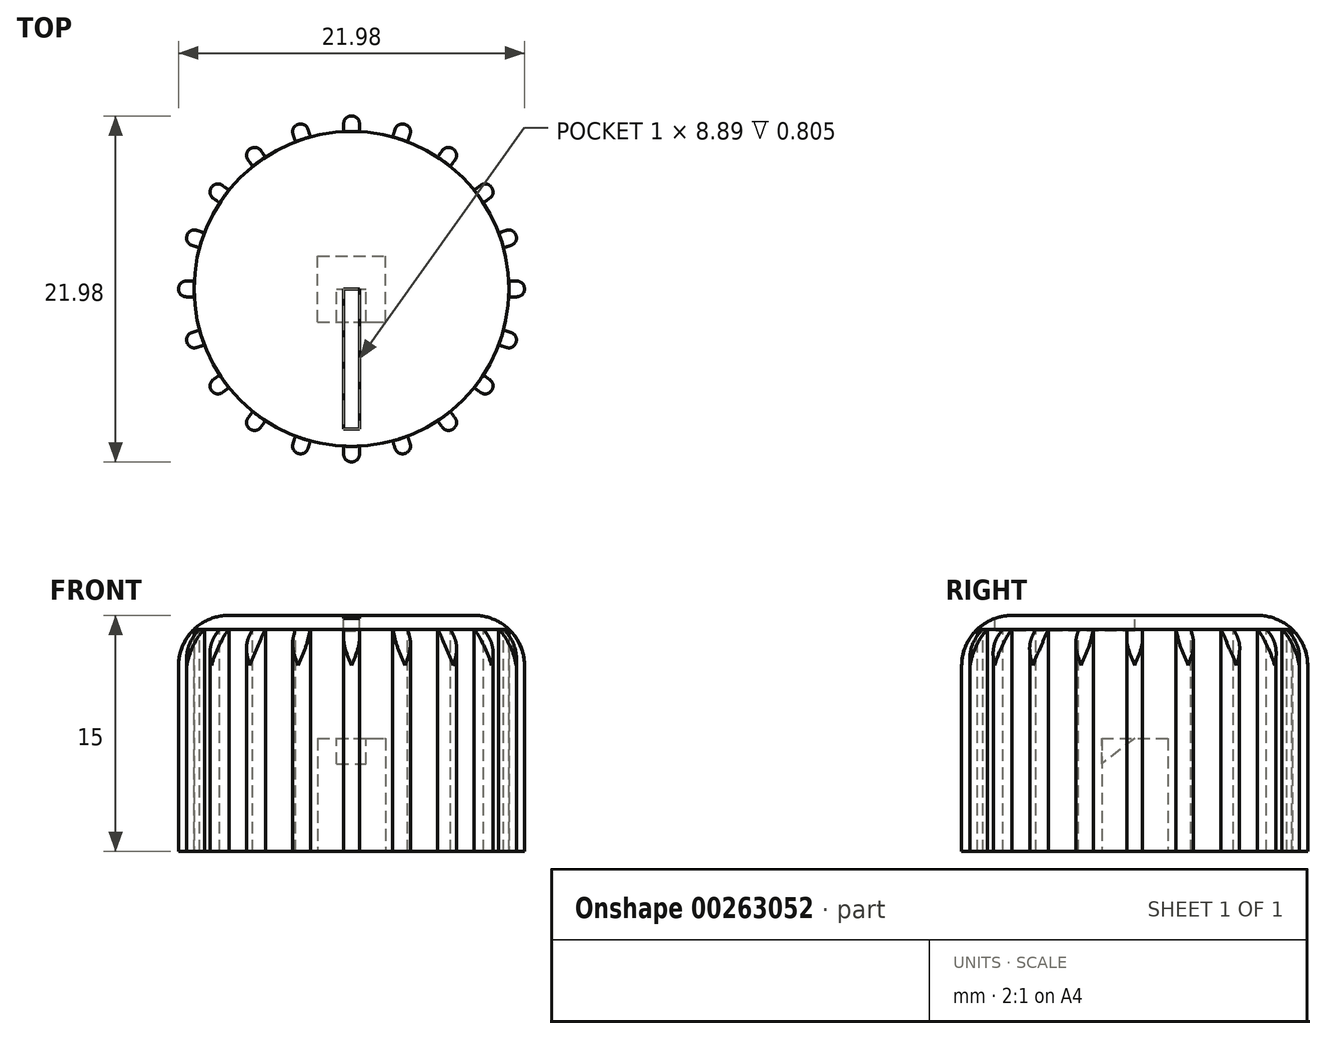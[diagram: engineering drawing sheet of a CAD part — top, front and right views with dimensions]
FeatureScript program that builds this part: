
annotation { "Feature Type Name" : "Feature", "Feature Type Description" : "" }
export const myFeature = defineFeature(function(context is Context, id is Id, definition is map)
    precondition{}
    {
        {
            var Q0;
            Q0=qCreatedBy(makeId("Top.planeOp"),FACE);
            var sketch = newSketch(context, id + "F0", { "sketchPlane" : qUnion([Q0])});
            skCircle(sketch, "E0", {"center": v(0, 0) * mm, "radius": 10 * mm});
            skSolve(sketch);
        }
        {
            var Q0;
            Q0=makeQuery(id+"F0.imprint","IMPRINT",FACE,{"disambiguationData":[TD([[makeQuery(id+"F0.imprint","IMPRINT",EDGE,{"derivedFrom":sQuery(id+"F0.wireOp",EDGE,"E0")}),1.0]])]});
            extrude(context, id + "F1", {"entities" : qUnion([Q0]), "depth" : 15 * mm});
        }
        {
            var Q0;
            Q0=makeQuery(id+"F1.opExtrude","CAP_FACE",FACE,{"disambiguationData":[OSD([sQuery(id+"F0.wireOp",EDGE,"E0")])],"isStart":true});
            var sketch = newSketch(context, id + "F2", { "sketchPlane" : qUnion([Q0])});
            skLineSegment(sketch, "E1.bottom", {"start": v(-2.16, 2.1) * mm, "end": v(2.16, 2.1) * mm});
            skLineSegment(sketch, "E1.top", {"start": v(-2.16, -2.1) * mm, "end": v(2.16, -2.1) * mm});
            skLineSegment(sketch, "E1.left", {"start": v(-2.16, 2.1) * mm, "end": v(-2.16, -2.1) * mm});
            skLineSegment(sketch, "E1.right", {"start": v(2.16, 2.1) * mm, "end": v(2.16, -2.1) * mm});
            skPoint(sketch, "E2", {"position": v(0, 2.1) * mm});
            skPoint(sketch, "E3", {"position": v(2.16, 0) * mm});
            skLineSegment(sketch, "E4.bottom", {"start": v(-0.94, 2.1) * mm, "end": v(0.94, 2.1) * mm});
            skLineSegment(sketch, "E4.top", {"start": v(-0.94, 0) * mm, "end": v(0.94, 0) * mm});
            skLineSegment(sketch, "E4.left", {"start": v(-0.94, 2.1) * mm, "end": v(-0.94, 0) * mm});
            skLineSegment(sketch, "E4.right", {"start": v(0.94, 2.1) * mm, "end": v(0.94, 0) * mm});
            skPoint(sketch, "E5", {"position": v(0, 0) * mm});
            skSolve(sketch);
        }
        {
            var Q0;
            Q0=makeQuery(id+"F2.imprint","IMPRINT",FACE,{"disambiguationData":[TD([[makeQuery(id+"F2.imprint","IMPRINT",EDGE,{"derivedFrom":sQuery(id+"F2.wireOp",EDGE,"E1.top")}),1.0]])]});
            extrude(context, id + "F3", {"entities" : qUnion([Q0]), "operationType" : NewBodyOperationType.REMOVE, "oppositeDirection" : true, "depth" : 1.63 * mm});
        }
        {
            var Q0;
            Q0=makeQuery(id+"F3.boolean.opBoolean","COPY",FACE,{"derivedFrom":makeQuery(id+"F3.opExtrude","CAP_FACE",FACE,{"disambiguationData":[OSD([sQuery(id+"F2.wireOp",EDGE,"E1.bottom"),sQuery(id+"F2.wireOp",EDGE,"E1.top"),sQuery(id+"F2.wireOp",EDGE,"E1.left"),sQuery(id+"F2.wireOp",EDGE,"E1.right"),sQuery(id+"F2.wireOp",EDGE,"E4.top"),sQuery(id+"F2.wireOp",EDGE,"E4.left"),sQuery(id+"F2.wireOp",EDGE,"E4.right")])],"isStart":false})});
            var sketch = newSketch(context, id + "F4", { "sketchPlane" : qUnion([Q0])});
            skLineSegment(sketch, "E6.bottom", {"start": v(-2.16, -2.1) * mm, "end": v(2.16, -2.1) * mm});
            skLineSegment(sketch, "E6.top", {"start": v(-2.16, 2.1) * mm, "end": v(2.16, 2.1) * mm});
            skLineSegment(sketch, "E6.left", {"start": v(-2.16, -2.1) * mm, "end": v(-2.16, 2.1) * mm});
            skLineSegment(sketch, "E6.right", {"start": v(2.16, -2.1) * mm, "end": v(2.16, 2.1) * mm});
            skSolve(sketch);
        }
        {
            var Q0;
            Q0=makeQuery(id+"F4.imprint","IMPRINT",FACE,{"disambiguationData":[TD([[makeQuery(id+"F4.imprint","IMPRINT",EDGE,{"derivedFrom":makeQuery(id+"F3.boolean.opBoolean","COPY",EDGE,{"derivedFrom":makeQuery(id+"F3.opExtrude","CAP_EDGE",EDGE,{"disambiguationData":[OSD([sQuery(id+"F2.wireOp",EDGE,"E4.top")])],"isStart":false})})}),1.0]])]});
            var Q1;
            Q1=makeQuery(id+"F4.imprint","IMPRINT",FACE,{"disambiguationData":[TD([[makeQuery(id+"F4.imprint","IMPRINT",EDGE,{"derivedFrom":sQuery(id+"F4.wireOp",EDGE,"E6.bottom")}),1.0]])]});
            extrude(context, id + "F5", {"entities" : qUnion([Q0, Q1]), "operationType" : NewBodyOperationType.REMOVE, "oppositeDirection" : true, "depth" : 5.56 * mm});
        }
        {
            var Q0;
            Q0=makeQuery(id+"F5.boolean.opBoolean","COPY",FACE,{"derivedFrom":makeQuery(id+"F5.opExtrude","CAP_FACE",FACE,{"disambiguationData":[OSD([sQuery(id+"F4.wireOp",EDGE,"E6.bottom"),sQuery(id+"F4.wireOp",EDGE,"E6.top"),sQuery(id+"F4.wireOp",EDGE,"E6.left"),sQuery(id+"F4.wireOp",EDGE,"E6.right")])],"isStart":false})});
            var sketch = newSketch(context, id + "F6", { "sketchPlane" : qUnion([Q0])});
            skSolve(sketch);
        }
        {
            var Q0;
            Q0=makeQuery(id+"F6.imprint","IMPRINT",FACE,{"disambiguationData":[TD([[makeQuery(id+"F6.imprint","IMPRINT",EDGE,{"derivedFrom":makeQuery(id+"F5.boolean.opBoolean","COPY",EDGE,{"derivedFrom":makeQuery(id+"F5.opExtrude","CAP_EDGE",EDGE,{"disambiguationData":[OSD([sQuery(id+"F4.wireOp",EDGE,"E6.bottom")])],"isStart":false})})}),1.0]])]});
            var sketch = newSketch(context, id + "F7", { "sketchPlane" : qUnion([Q0])});
            skLineSegment(sketch, "E7.0", {"start": v(0.94, 2.1) * mm, "end": v(0.94, 0) * mm});
            skLineSegment(sketch, "E8.0", {"start": v(-0.94, 0) * mm, "end": v(0.94, 0) * mm});
            skLineSegment(sketch, "E9.0", {"start": v(-0.94, 2.1) * mm, "end": v(-0.94, 0) * mm});
            skSolve(sketch);
        }
        {
            var Q0;
            Q0=makeQuery(id+"F3.boolean.opBoolean","COPY",FACE,{"derivedFrom":makeQuery(id+"F3.opExtrude","SWEPT_FACE",FACE,{"disambiguationData":[OSD([sQuery(id+"F2.wireOp",EDGE,"E4.top")])]})});
            var Q1;
            {var subQ0=sQuery(id+"F2.wireOp",EDGE,"E1.bottom");Q1=makeQuery(id+"F5.boolean.opBoolean","MERGE",FACE,{"derivedFrom":[makeQuery(id+"F3.boolean.opBoolean","COPY",FACE,{"derivedFrom":makeQuery(id+"F3.opExtrude","SWEPT_FACE",FACE,{"disambiguationData":[OSD([subQ0]),TDD([makeQuery(id+"F2.imprint","IMPRINT",EDGE,{"disambiguationData":[TD([[makeQuery(id+"F2.imprint","INTERSECT",VERTEX,{"derivedFrom":[subQ0,sQuery(id+"F2.wireOp",EDGE,"E1.left")]}),-1.0]])],"derivedFrom":subQ0})])]})}),makeQuery(id+"F3.boolean.opBoolean","COPY",FACE,{"derivedFrom":makeQuery(id+"F3.opExtrude","SWEPT_FACE",FACE,{"disambiguationData":[OSD([subQ0]),TDD([makeQuery(id+"F2.imprint","IMPRINT",EDGE,{"disambiguationData":[TD([[makeQuery(id+"F2.imprint","INTERSECT",VERTEX,{"derivedFrom":[subQ0,sQuery(id+"F2.wireOp",EDGE,"E1.right")]}),1.0]])],"derivedFrom":subQ0})])]})}),makeQuery(id+"F5.opExtrude","SWEPT_FACE",FACE,{"disambiguationData":[OSD([sQuery(id+"F4.wireOp",EDGE,"E6.top")])]})]});}
            extrude(context, id + "F8", {"entities" : qUnion([Q0]), "operationType" : NewBodyOperationType.REMOVE, "endBound" : BoundingType.UP_TO_SURFACE, "oppositeDirection" : true, "endBoundEntityFace" : qUnion([Q1]), "depth" : 25.4 * mm});
        }
        {
            var Q0;
            {var subQ0=sQuery(id+"F7.wireOp",EDGE,"E7.0");Q0=makeQuery(id+"F7.imprint","IMPRINT",FACE,{"disambiguationData":[TD([[makeQuery(id+"F7.imprint","IMPRINT",EDGE,{"derivedFrom":subQ0}),-1.0]])]});}
            extrude(context, id + "F9", {"entities" : qUnion([Q0]), "operationType" : NewBodyOperationType.ADD, "depth" : 1.63 * mm});
        }
        {
            var Q0;
            Q0=makeQuery(id+"F9.opExtrude","SWEPT_FACE",FACE,{"disambiguationData":[OSD([sQuery(id+"F7.wireOp",EDGE,"E7.0")])]});
            var sketch = newSketch(context, id + "F10", { "sketchPlane" : qUnion([Q0])});
            skLineSegment(sketch, "E10", {"start": v(0, 7.19) * mm, "end": v(-2.1, 5.56) * mm});
            skLineSegment(sketch, "E11", {"start": v(-2.1, 5.56) * mm, "end": v(-2.1, 7.19) * mm});
            skLineSegment(sketch, "E12", {"start": v(-2.1, 7.19) * mm, "end": v(0, 7.19) * mm});
            skLineSegment(sketch, "E13", {"start": v(0, 5.56) * mm, "end": v(0, 7.19) * mm});
            skLineSegment(sketch, "E14", {"start": v(-2.1, 5.56) * mm, "end": v(0, 5.56) * mm});
            skSolve(sketch);
        }
        {
            var Q0;
            Q0=makeQuery(id+"F10.imprint","IMPRINT",FACE,{"disambiguationData":[TD([[makeQuery(id+"F10.imprint","IMPRINT",EDGE,{"derivedFrom":sQuery(id+"F10.wireOp",EDGE,"E10")}),1.0]])]});
            var Q1;
            Q1=makeQuery(id+"F5.boolean.opBoolean","MERGE",FACE,{"derivedFrom":[makeQuery(id+"F3.boolean.opBoolean","COPY",FACE,{"derivedFrom":makeQuery(id+"F3.opExtrude","SWEPT_FACE",FACE,{"disambiguationData":[OSD([sQuery(id+"F2.wireOp",EDGE,"E1.left")])]})}),makeQuery(id+"F5.opExtrude","SWEPT_FACE",FACE,{"disambiguationData":[OSD([sQuery(id+"F4.wireOp",EDGE,"E6.left")])]})]});
            extrude(context, id + "F11", {"entities" : qUnion([Q0]), "operationType" : NewBodyOperationType.REMOVE, "endBound" : BoundingType.UP_TO_SURFACE, "oppositeDirection" : true, "endBoundEntityFace" : qUnion([Q1]), "depth" : 25.4 * mm});
        }
        {
            var Q0;
            Q0=makeQuery(id+"F1.opExtrude","CAP_FACE",FACE,{"disambiguationData":[OSD([sQuery(id+"F0.wireOp",EDGE,"E0")])],"isStart":false});
            var sketch = newSketch(context, id + "F12", { "sketchPlane" : qUnion([Q0])});
            skLineSegment(sketch, "E15.bottom", {"start": v(-0.5, -8.9) * mm, "end": v(0.5, -8.9) * mm});
            skLineSegment(sketch, "E15.top", {"start": v(-0.5, 0) * mm, "end": v(0.5, 0) * mm});
            skLineSegment(sketch, "E15.left", {"start": v(-0.5, 0) * mm, "end": v(-0.5, -8.9) * mm});
            skLineSegment(sketch, "E15.right", {"start": v(0.5, 0) * mm, "end": v(0.5, -8.9) * mm});
            skPoint(sketch, "E16.positionSnap0", {"position": v(0, 0) * mm});
            skSolve(sketch);
        }
        {
            var Q0;
            Q0=makeQuery(id+"F12.imprint","IMPRINT",FACE,{"disambiguationData":[TD([[makeQuery(id+"F12.imprint","IMPRINT",EDGE,{"derivedFrom":sQuery(id+"F12.wireOp",EDGE,"E15.bottom")}),1.0]])]});
            extrude(context, id + "F13", {"entities" : qUnion([Q0]), "operationType" : NewBodyOperationType.REMOVE, "oppositeDirection" : true, "depth" : 1 * mm});
        }
        {
            var Q0;
            Q0=makeQuery(id+"F1.opExtrude","CAP_FACE",FACE,{"disambiguationData":[OSD([sQuery(id+"F0.wireOp",EDGE,"E0")])],"isStart":false});
            var sketch = newSketch(context, id + "F14", { "sketchPlane" : qUnion([Q0])});
            skPoint(sketch, "E17.firstSnap0", {"position": v(-0.5, -4.45) * mm});
            skLineSegment(sketch, "E17.bottom", {"start": v(-0.5, -9.99) * mm, "end": v(0.5, -9.99) * mm});
            skLineSegment(sketch, "E17.top", {"start": v(-0.5, -10.99) * mm, "end": v(0.5, -10.99) * mm});
            skLineSegment(sketch, "E17.left", {"start": v(-0.5, -9.99) * mm, "end": v(-0.5, -10.99) * mm});
            skLineSegment(sketch, "E17.right", {"start": v(0.5, -9.99) * mm, "end": v(0.5, -10.99) * mm});
            skCircle(sketch, "E18.0.0", {"center": v(0, 0) * mm, "radius": 10 * mm});
            skSolve(sketch);
        }
        {
            var Q0;
            Q0=makeQuery(id+"F14.imprint","IMPRINT",FACE,{"disambiguationData":[TD([[makeQuery(id+"F14.imprint","IMPRINT",EDGE,{"derivedFrom":sQuery(id+"F14.wireOp",EDGE,"E17.top")}),1.0]])]});
            var Q1;
            Q1=makeQuery(id+"F1.opExtrude","CAP_FACE",FACE,{"disambiguationData":[OSD([sQuery(id+"F0.wireOp",EDGE,"E0")])],"isStart":true});
            extrude(context, id + "F15", {"entities" : qUnion([Q0]), "endBound" : BoundingType.UP_TO_SURFACE, "oppositeDirection" : true, "endBoundEntityFace" : qUnion([Q1]), "depth" : 25.4 * mm});
        }
        {
            var Q0;
            Q0=makeQuery(id+"F15.opExtrude","SWEPT_EDGE",EDGE,{"disambiguationData":[OSD([sQuery(id+"F14.wireOp",EDGE,"E17.top"),sQuery(id+"F14.wireOp",EDGE,"E17.right")])]});
            var Q1;
            Q1=makeQuery(id+"F15.opExtrude","SWEPT_EDGE",EDGE,{"disambiguationData":[OSD([sQuery(id+"F14.wireOp",EDGE,"E17.top"),sQuery(id+"F14.wireOp",EDGE,"E17.left")])]});
            fillet(context, id + "F16", {"entities" : qUnion([Q0, Q1]), "radius" : .5 * mm, "tangentPropagation" : true, "allowEdgeOverflow" : false});
        }
        {
            var Q0;
            Q0=qCreatedBy(makeId("Front.planeOp"),FACE);
            var sketch = newSketch(context, id + "F17", { "sketchPlane" : qUnion([Q0])});
            skLineSegment(sketch, "E19.0", {"start": v(-10, 15) * mm, "end": v(10, 15) * mm});
            skLineSegment(sketch, "E20", {"start": v(0, 15) * mm, "end": v(0, 0) * mm, "construction": true});
            skSolve(sketch);
        }
        {
            var Q0;
            Q0=makeQuery(id+"F15.opExtrude","SWEPT_BODY",BODY,{"disambiguationData":[OSD([sQuery(id+"F0.wireOp",EDGE,"E0"),sQuery(id+"F14.wireOp",EDGE,"E17.top"),sQuery(id+"F14.wireOp",EDGE,"E17.left"),sQuery(id+"F14.wireOp",EDGE,"E17.right")])]});
            var Q1;
            Q1=sQuery(id+"F17.wireOp",EDGE,"E20");
            circularPattern(context, id + "F18", {"entities" : qUnion([Q0]), "axis" : qUnion([Q1]), "angle" : 360 * degree, "instanceCount" : 20, "equalSpace" : true});
        }
        {
            var Q0;
            Q0=qCreatedBy(makeId("Front.planeOp"),FACE);
            var sketch = newSketch(context, id + "F19", { "sketchPlane" : qUnion([Q0])});
            skPoint(sketch, "E21.0", {"position": v(-10.99, 15) * mm});
            skLineSegment(sketch, "E22", {"start": v(-10.99, 0) * mm, "end": v(-10.99, 15) * mm});
            skLineSegment(sketch, "E23.0", {"start": v(-10, 15) * mm, "end": v(10, 15) * mm});
            skArc(sketch, "E24", {"start": v(-7.8, 15) * mm, "mid": v(-10.06, 14.07) * mm, "end": v(-10.99, 11.82) * mm});
            skLineSegment(sketch, "E25", {"start": v(-10.99, 11.82) * mm, "end": v(-14.2, 11.82) * mm});
            skLineSegment(sketch, "E26", {"start": v(-14.2, 11.82) * mm, "end": v(-14.2, 17.5) * mm});
            skLineSegment(sketch, "E27", {"start": v(-14.2, 17.5) * mm, "end": v(-7.8, 17.5) * mm});
            skLineSegment(sketch, "E28", {"start": v(-7.8, 17.5) * mm, "end": v(-7.8, 15) * mm});
            skSolve(sketch);
        }
        {
            var Q0;
            Q0=makeQuery(id+"F19.imprint","IMPRINT",FACE,{"disambiguationData":[TD([[makeQuery(id+"F19.imprint","IMPRINT",EDGE,{"derivedFrom":sQuery(id+"F19.wireOp",EDGE,"E24")}),-1.0]])]});
            var Q1;
            Q1=sQuery(id+"F17.wireOp",EDGE,"E20");
            revolve(context, id + "F20", {"operationType" : NewBodyOperationType.REMOVE, "entities" : qUnion([Q0]), "axis" : qUnion([Q1]), "revolveType" : RevolveType.FULL, "oppositeDirection" : true});
        }
    });
